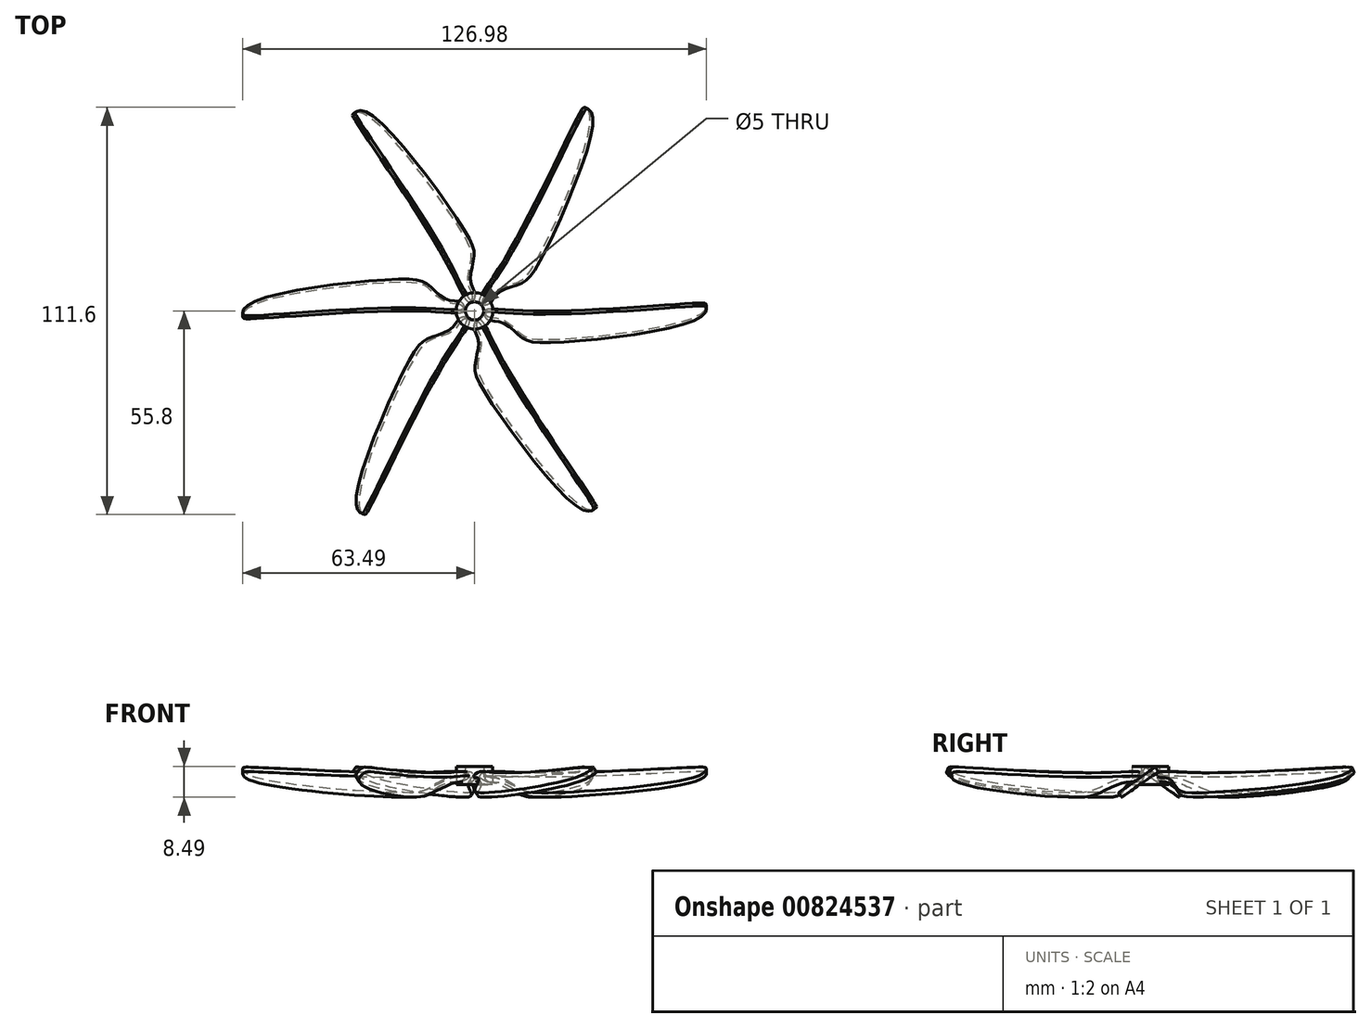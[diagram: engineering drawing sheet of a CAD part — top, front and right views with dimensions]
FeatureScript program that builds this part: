
annotation { "Feature Type Name" : "Feature", "Feature Type Description" : "" }
export const myFeature = defineFeature(function(context is Context, id is Id, definition is map)
    precondition{}
    {
        {
            var Q0;
            Q0=qCreatedBy(makeId("Top.planeOp"),FACE);
            var sketch = newSketch(context, id + "F0", { "sketchPlane" : qUnion([Q0])});
            skCircle(sketch, "E0", {"center": v(0, 0) * mm, "radius": 2.5 * mm});
            skCircle(sketch, "E1", {"center": v(0, 0) * mm, "radius": 5 * mm});
            skSolve(sketch);
        }
        {
            var Q0;
            Q0=qCreatedBy(makeId("Top.planeOp"),FACE);
            var sketch = newSketch(context, id + "F1", { "sketchPlane" : qUnion([Q0])});
            skLineSegment(sketch, "E2", {"start": v(0, 0) * mm, "end": v(-63.5, 0) * mm, "construction": true});
            skFitSpline(sketch, "E3", {"points": [v(-3.72, 1.92) * mm, v(-7.38, 2.7) * mm, v(-12.49, 7.46) * mm, v(-19.43, 9.57) * mm, v(-61.35, 1.47) * mm, v(-63.4, -2.2) * mm, v(-61.61, -2.67) * mm, v(-15.65, 0) * mm, v(-2.82, 0) * mm, v(-3.72, 1.92) * mm]});
            skSolve(sketch);
        }
        {
            var Q0;
            Q0=makeQuery(id+"F1.imprint","IMPRINT",FACE,{"disambiguationData":[TD([[makeQuery(id+"F1.imprint","IMPRINT",EDGE,{"derivedFrom":sQuery(id+"F1.wireOp",EDGE,"E3")}),1.0]])]});
            extrude(context, id + "F2", {"entities" : qUnion([Q0]), "depth" : 1.5 * mm, "offsetDistance" : 25 * mm});
        }
        {
            var Q0;
            Q0 = qSketchRegion(id + "F0", true);
            extrude(context, id + "F3", {"entities" : qUnion([Q0]), "depth" : 3 * mm, "offsetDistance" : 25 * mm, "hasSecondDirection" : true, "secondDirectionOppositeDirection" : true, "secondDirectionDepth" : 2 * mm});
        }
        {
            var Q0;
            Q0=qCreatedBy(makeId("Front.planeOp"),FACE);
            var sketch = newSketch(context, id + "F4", { "sketchPlane" : qUnion([Q0])});
            skLineSegment(sketch, "E4", {"start": v(0, 0) * mm, "end": v(0, 19.75) * mm, "construction": true});
            skSolve(sketch);
        }
        {
            var Q0;
            Q0=makeQuery(id+"F2.opExtrude","SWEPT_BODY",BODY,{"disambiguationData":[OSD([sQuery(id+"F1.wireOp",EDGE,"E3")])]});
            var Q1;
            Q1=sQuery(id+"F1.wireOp",EDGE,"E2");
            transform(context, id + "F5", {"entities" : qUnion([Q0]), "transformType" : TransformType.ROTATION, "transformAxis" : qUnion([Q1]), "angle" : 35 * degree, "makeCopy" : false});
        }
        {
            var Q0;
            Q0=makeQuery(id+"F2.opExtrude","SWEPT_BODY",BODY,{"disambiguationData":[OSD([sQuery(id+"F1.wireOp",EDGE,"E3")])]});
            var Q1;
            Q1=sQuery(id+"F4.wireOp",EDGE,"E4");
            circularPattern(context, id + "F6", {"entities" : qUnion([Q0]), "axis" : qUnion([Q1]), "angle" : 360 * degree, "instanceCount" : 6, "equalSpace" : true});
        }
    });
